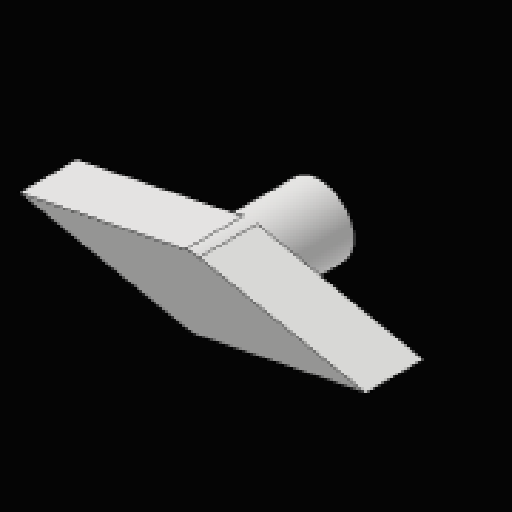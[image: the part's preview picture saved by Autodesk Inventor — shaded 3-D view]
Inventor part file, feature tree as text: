
AUTODESK INVENTOR PART (.ipt)
format: ipt  version: 2023.2 (Build 272271030, 271C)  size: 99,840 bytes
history: native  units: mm
features: extrude x2, sketch x2, projected_geometry x1
ambient origin geometry x8: Origin, YZ Plane, XZ Plane, XY Plane, X Axis, Y Axis, Z Axis, Center Point
bodies: Solid1 (feature_tree)
feature tree (5):
  extrude  "Extrusion1"  Depth=9.0mm TaperAngle=0.0deg
  extrude  "Extrusion2"  Depth=5.0mm TaperAngle=0.0deg
  sketch  "Sketch1"  dims[d0=7.0mm d1=9.0mm d2=0.0mm]
  sketch  "Sketch2"  dims[d3=30.0mm d4=5.0mm d5=0.0mm d6=0.5mm d7=0.872665mm d8=0.5mm d9=0.872665mm]
  projected_geometry  "Projected Loop1"
